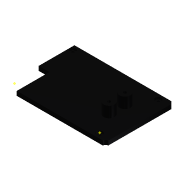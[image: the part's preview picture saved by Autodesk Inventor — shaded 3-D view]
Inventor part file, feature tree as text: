
AUTODESK INVENTOR PART (.ipt)
format: ipt  version: 2013 (Build 170138000, 138)  size: 145,408 bytes
history: native  units: in
note: dims shown in document units (in); Inventor stores cm internally (conversion verified against a paired STEP export)
features: extrude x5, sketch x5, other x2, hole x1
ambient origin geometry x8: Origin, YZ Plane, XZ Plane, XY Plane, X Axis, Y Axis, Z Axis, Center Point
bodies: Solid1 (feature_tree)
feature tree (13):
  extrude  "Extrusion1"  Depth=1.6in
  hole  "Hole2"  [1 undecoded]
  extrude  "Extrusion9"  Depth=0.063in
  extrude  "Extrusion10"  Depth=0.25in
  other  "Work Point1"
  other  "Work Point2"
  extrude  "Extrusion11"  Depth=0.0625in
  extrude  "Extrusion12"  Depth=0.0625in
  sketch  "Sketch1"  dims[d0=2.8in d1=1.6in]
  sketch  "Sketch8"  dims[d2=0.1in d3=0.0in d75=0.063in]
  sketch  "Sketch9"  dims[d76=0.063in d77=0.063in]
  sketch  "Sketch10"  dims[d78=0.063in d79=0.25in]
  sketch  "Sketch12"  dims[d80=0.063in d81=0.75in d82=0.1378in d83=0.05in d84=0.5635in d85=1.0in d86=0.8108in d87=0.0625in d89=0.0625in d90=0.0625in d91=0.0625in d92=1.0in d93=0.0in d95=0.25in d96=0.25in d102=0.25in d103=0.0in d106=0.0689in d107=0.0689in d108=2.0in d118=1.0in d119=0.0in d120=0.1969in d121=0.0in d122=0.531in d123=0.531in d125=0.372in d126=0.614in d128=0.8125in d129=0.25in]
note: 1 required parameter value undecoded (feature->parameter linkage not recoverable at this tier; creation-order binding heuristic only, values carry confidence <= 0.55)
